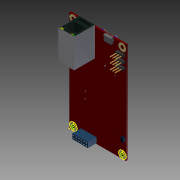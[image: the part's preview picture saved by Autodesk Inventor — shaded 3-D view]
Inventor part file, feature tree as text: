
AUTODESK INVENTOR PART (.ipt)
format: ipt  version: 2015 (Build 190159000, 159)  size: 3,255,808 bytes
history: native  units: in
note: dims shown in document units (in); Inventor stores cm internally (conversion verified against a paired STEP export)
features: imported_body x109, extrude x96, projected_geometry x25, other x14, sketch x3
ambient origin geometry x8: Origin, YZ Plane, XZ Plane, XY Plane, X Axis, Y Axis, Z Axis, Center Point
bodies: Body1 (feature_tree), Body2 (feature_tree), Body3 (feature_tree), Body4 (feature_tree), Body5 (feature_tree), Body6 (feature_tree), Body7 (feature_tree), Body8 (feature_tree), Body9 (feature_tree), Body10 (feature_tree), Body11 (feature_tree), Body12 (feature_tree), Body13 (feature_tree), Body14 (feature_tree), Body15 (feature_tree), Body16 (feature_tree), Body17 (feature_tree), Body18 (feature_tree), Body19 (feature_tree), Body20 (feature_tree), Body21 (feature_tree), Body22 (feature_tree), Body23 (feature_tree), Body24 (feature_tree), Body25 (feature_tree), Body26 (feature_tree), Body27 (feature_tree), Body28 (feature_tree), Body29 (feature_tree), Body30 (feature_tree), Body31 (feature_tree), Body32 (feature_tree), Body33 (feature_tree), Body34 (feature_tree), Body35 (feature_tree), Body36 (feature_tree), Body37 (feature_tree), Body38 (feature_tree), Body39 (feature_tree), Body40 (feature_tree), Body41 (feature_tree), Body42 (feature_tree), Body43 (feature_tree), Body44 (feature_tree), Body45 (feature_tree), Body46 (feature_tree), Body47 (feature_tree), Body48 (feature_tree), Body49 (feature_tree), Body50 (feature_tree), Body51 (feature_tree), Body52 (feature_tree), Body53 (feature_tree), Body54 (feature_tree), Body55 (feature_tree), Body56 (feature_tree), Body57 (feature_tree), Body58 (feature_tree), Body59 (feature_tree), Body60 (feature_tree), Body61 (feature_tree), Body62 (feature_tree), Body63 (feature_tree), Body64 (feature_tree), Body65 (feature_tree), Body66 (feature_tree), Body67 (feature_tree), Body68 (feature_tree), Body69 (feature_tree), Body70 (feature_tree), Body71 (feature_tree), Body72 (feature_tree), Body73 (feature_tree), Body74 (feature_tree), Body75 (feature_tree), Body76 (feature_tree), Body77 (feature_tree), Body78 (feature_tree), Body79 (feature_tree), Body80 (feature_tree), Body81 (feature_tree), Body82 (feature_tree), Body83 (feature_tree), Body84 (feature_tree), Body85 (feature_tree), Body86 (feature_tree), Body87 (feature_tree), Body88 (feature_tree), Body89 (feature_tree), Body90 (feature_tree), Body91 (feature_tree), Body92 (feature_tree), Body93 (feature_tree), Body94 (feature_tree), Body95 (feature_tree), Body96 (feature_tree), Body97 (feature_tree), Body98 (feature_tree), Body99 (feature_tree), Body100 (feature_tree), Body101 (feature_tree), Body102 (feature_tree), Body103 (feature_tree), Body104 (feature_tree), Body105 (feature_tree), Body106 (feature_tree), Body107 (feature_tree), Body108 (feature_tree), Body109 (feature_tree)
feature tree (247):
  other  "Board"
  other  "Repaired Geometry1"
  sketch  "Sketch1"  dims[d3=0.3009in d4=0.0005in]
  sketch  "Sketch2"  dims[d5=0.0653in d6=0.0653in d7=0.0653in d8=0.0653in d9=0.0653in d10=0.0653in d11=0.0653in d12=0.0653in d13=0.0098in d14=0.0098in d15=1.1299in d16=1.1299in d17=1.7402in d18=0.0404in]
  extrude  "Extruded_664"  Depth=0.0005in
  other  "Open CASCADE STEP translator 6.2 1.226.1.1"
  extrude  "Extruded_665"  Depth=1.1299in
  extrude  "Extruded_666"  Depth=1.1299in
  extrude  "Extruded_667"  Depth=1.1299in
  extrude  "Extruded_668"  Depth=1.1299in
  extrude  "Extruded_669"  Depth=1.1299in
  extrude  "Extruded_670"  Depth=1.1299in
  extrude  "Extruded_671"  Depth=1.1299in
  extrude  "Extruded_672"  Depth=1.1299in
  extrude  "Extruded_673"  Depth=1.1299in
  extrude  "Extruded_674"  Depth=1.1299in
  extrude  "Extruded_675"  Depth=1.1299in
  extrude  "Extruded_676"  Depth=1.1299in
  extrude  "Extruded_677"  Depth=1.1299in
  extrude  "Extruded_678"  [1 undecoded]
  extrude  "Extruded_679"  [1 undecoded]
  extrude  "Extruded_680"  [1 undecoded]
  extrude  "Extruded_681"  [1 undecoded]
  extrude  "Extruded_682"  [1 undecoded]
  extrude  "Extruded_683"  [1 undecoded]
  extrude  "Extruded_684"  [1 undecoded]
  extrude  "Extruded_685"  [1 undecoded]
  extrude  "Extruded_686"  [1 undecoded]
  extrude  "Extruded_687"  [1 undecoded]
  extrude  "Extruded_688"  [1 undecoded]
  extrude  "Extruded_689"  [1 undecoded]
  extrude  "Extruded_690"  [1 undecoded]
  extrude  "Extruded_691"  [1 undecoded]
  extrude  "Extruded_692"  [1 undecoded]
  extrude  "Extruded_693"  [1 undecoded]
  extrude  "Extruded_694"  [1 undecoded]
  extrude  "Extruded_695"  [1 undecoded]
  extrude  "Extruded_696"  [1 undecoded]
  extrude  "Extruded_697"  [1 undecoded]
  extrude  "Extruded_698"  [1 undecoded]
  extrude  "Extruded_699"  [1 undecoded]
  extrude  "Extruded_700"  [1 undecoded]
  extrude  "Extruded_701"  [1 undecoded]
  extrude  "Extruded_702"  [1 undecoded]
  extrude  "Extruded_703"  [1 undecoded]
  extrude  "Extruded_704"  [1 undecoded]
  other  "Cylinder_24"
  other  "Cylinder_25"
  other  "Cylinder_26"
  other  "Cylinder_27"
  other  "Cylinder_28"
  extrude  "Extruded_705"  [1 undecoded]
  other  "Cylinder_29"
  other  "Cylinder_30"
  extrude  "Extruded_706"  [1 undecoded]
  extrude  "Extruded_707"  [1 undecoded]
  extrude  "Extruded_708"  [1 undecoded]
  extrude  "Extruded_709"  [1 undecoded]
  extrude  "Extruded_710"  [1 undecoded]
  extrude  "Extruded_711"  [1 undecoded]
  extrude  "Extruded_712"  [1 undecoded]
  extrude  "Extruded_713"  [1 undecoded]
  extrude  "Extruded_714"  [1 undecoded]
  extrude  "Extruded_715"  [1 undecoded]
  extrude  "Extruded_716"  [1 undecoded]
  extrude  "Extruded_717"  [1 undecoded]
  extrude  "Extruded_718"  [1 undecoded]
  extrude  "Extruded_719"  [1 undecoded]
  extrude  "Extruded_720"  [1 undecoded]
  extrude  "Extruded_721"  [1 undecoded]
  extrude  "Extruded_722"  [1 undecoded]
  other  "Open CASCADE STEP translator 6.2 1.229.1.1"
  extrude  "Extruded_723"  [1 undecoded]
  extrude  "Extruded_724"  [1 undecoded]
  extrude  "Extruded_725"  [1 undecoded]
  extrude  "Extruded_726"  [1 undecoded]
  extrude  "Extruded_727"  [1 undecoded]
  extrude  "Extruded_728"  [1 undecoded]
  extrude  "Extruded_729"  [1 undecoded]
  extrude  "Extruded_730"  [1 undecoded]
  extrude  "Extruded_731"  [1 undecoded]
  extrude  "Extruded_732"  [1 undecoded]
  extrude  "Extruded_733"  [1 undecoded]
  extrude  "Extruded_734"  [1 undecoded]
  other  "61082101400lf"
  other  "61082101400lf_1"
  extrude  "Extruded_735"  [1 undecoded]
  extrude  "Extruded_837"  [1 undecoded]
  extrude  "Extruded_838"  [1 undecoded]
  extrude  "Extruded_839"  [1 undecoded]
  extrude  "Extruded_840"  [1 undecoded]
  extrude  "Extruded_841"  [1 undecoded]
  extrude  "Extruded_842"  [1 undecoded]
  extrude  "Extruded_1006"  [1 undecoded]
  extrude  "Extruded_1007"  [1 undecoded]
  other  "Cylinder_44"
  extrude  "Extruded_1038"  [1 undecoded]
  extrude  "Extruded_1039"  [1 undecoded]
  extrude  "Extruded_1040"  [1 undecoded]
  extrude  "Extruded_1041"  [1 undecoded]
  extrude  "Extruded_1042"  [1 undecoded]
  extrude  "Extruded_1043"  [1 undecoded]
  extrude  "Extruded_1044"  [1 undecoded]
  extrude  "Extruded_1067"  [1 undecoded]
  extrude  "Extruded_1068"  [1 undecoded]
  extrude  "Extruded_1069"  [1 undecoded]
  extrude  "Extruded_1070"  [1 undecoded]
  extrude  "Extruded_1071"  [1 undecoded]
  extrude  "Extruded_1072"  [1 undecoded]
  extrude  "Extruded_1073"  [1 undecoded]
  extrude  "Extruded_1074"  [1 undecoded]
  extrude  "Extruded_1111"  [1 undecoded]
  sketch  "3D Sketch1"
  projected_geometry  "Projected Loop1"
  projected_geometry  "Projected Loop2"
  projected_geometry  "Projected Loop3"
  projected_geometry  "Projected Loop4"
  projected_geometry  "Projected Loop5"
  projected_geometry  "Projected Loop6"
  projected_geometry  "Projected Loop7"
  projected_geometry  "Projected Loop8"
  projected_geometry  "Projected Loop9"
  projected_geometry  "Projected Loop10"
  projected_geometry  "Projected Loop11"
  projected_geometry  "Projected Loop12"
  projected_geometry  "Projected Loop13"
  projected_geometry  "Projected Loop14"
  projected_geometry  "Projected Loop15"
  projected_geometry  "Projected Loop16"
  projected_geometry  "Projected Loop17"
  projected_geometry  "Projected Loop18"
  projected_geometry  "Projected Loop19"
  projected_geometry  "Projected Loop20"
  projected_geometry  "Projected Loop21"
  projected_geometry  "Projected Loop22"
  projected_geometry  "Projected Loop23"
  projected_geometry  "Projected Loop24"
  projected_geometry  "Projected Loop25"
  imported_body  "Base1"
  imported_body  "Base675"
  imported_body  "Base676"
  imported_body  "Base677"
  imported_body  "Base678"
  imported_body  "Base679"
  imported_body  "Base680"
  imported_body  "Base681"
  imported_body  "Base682"
  imported_body  "Base683"
  imported_body  "Base684"
  imported_body  "Base685"
  imported_body  "Base686"
  imported_body  "Base687"
  imported_body  "Base688"
  imported_body  "Base689"
  imported_body  "Base690"
  imported_body  "Base691"
  imported_body  "Base692"
  imported_body  "Base693"
  imported_body  "Base694"
  imported_body  "Base695"
  imported_body  "Base696"
  imported_body  "Base697"
  imported_body  "Base698"
  imported_body  "Base699"
  imported_body  "Base700"
  imported_body  "Base701"
  imported_body  "Base702"
  imported_body  "Base703"
  imported_body  "Base704"
  imported_body  "Base705"
  imported_body  "Base706"
  imported_body  "Base707"
  imported_body  "Base708"
  imported_body  "Base709"
  imported_body  "Base710"
  imported_body  "Base711"
  imported_body  "Base712"
  imported_body  "Base713"
  imported_body  "Base714"
  imported_body  "Base715"
  imported_body  "Base716"
  imported_body  "Base732"
  imported_body  "Base733"
  imported_body  "Base734"
  imported_body  "Base735"
  imported_body  "Base736"
  imported_body  "Base737"
  imported_body  "Base738"
  imported_body  "Base739"
  imported_body  "Base740"
  imported_body  "Base741"
  imported_body  "Base742"
  imported_body  "Base743"
  imported_body  "Base744"
  imported_body  "Base745"
  imported_body  "Base746"
  imported_body  "Base747"
  imported_body  "Base748"
  imported_body  "Base749"
  imported_body  "Base750"
  imported_body  "Base751"
  imported_body  "Base752"
  imported_body  "Base753"
  imported_body  "Base754"
  imported_body  "Base755"
  imported_body  "Base756"
  imported_body  "Base757"
  imported_body  "Base758"
  imported_body  "Base759"
  imported_body  "Base760"
  imported_body  "Base761"
  imported_body  "Base762"
  imported_body  "Base763"
  imported_body  "Base764"
  imported_body  "Base765"
  imported_body  "Base766"
  imported_body  "Base767"
  imported_body  "Base768"
  imported_body  "Base769"
  imported_body  "Base770"
  imported_body  "Base771"
  imported_body  "Base772"
  imported_body  "Base874"
  imported_body  "Base875"
  imported_body  "Base876"
  imported_body  "Base877"
  imported_body  "Base878"
  imported_body  "Base879"
  imported_body  "Base1043"
  imported_body  "Base1044"
  imported_body  "Base1088"
  imported_body  "Base1089"
  imported_body  "Base1090"
  imported_body  "Base1091"
  imported_body  "Base1092"
  imported_body  "Base1093"
  imported_body  "Base1094"
  imported_body  "Base1095"
  imported_body  "Base1119"
  imported_body  "Base1120"
  imported_body  "Base1121"
  imported_body  "Base1122"
  imported_body  "Base1123"
  imported_body  "Base1124"
  imported_body  "Base1125"
  imported_body  "Base1126"
  imported_body  "Base1163"
note: 82 required parameter values undecoded (feature->parameter linkage not recoverable at this tier; creation-order binding heuristic only, values carry confidence <= 0.55)
